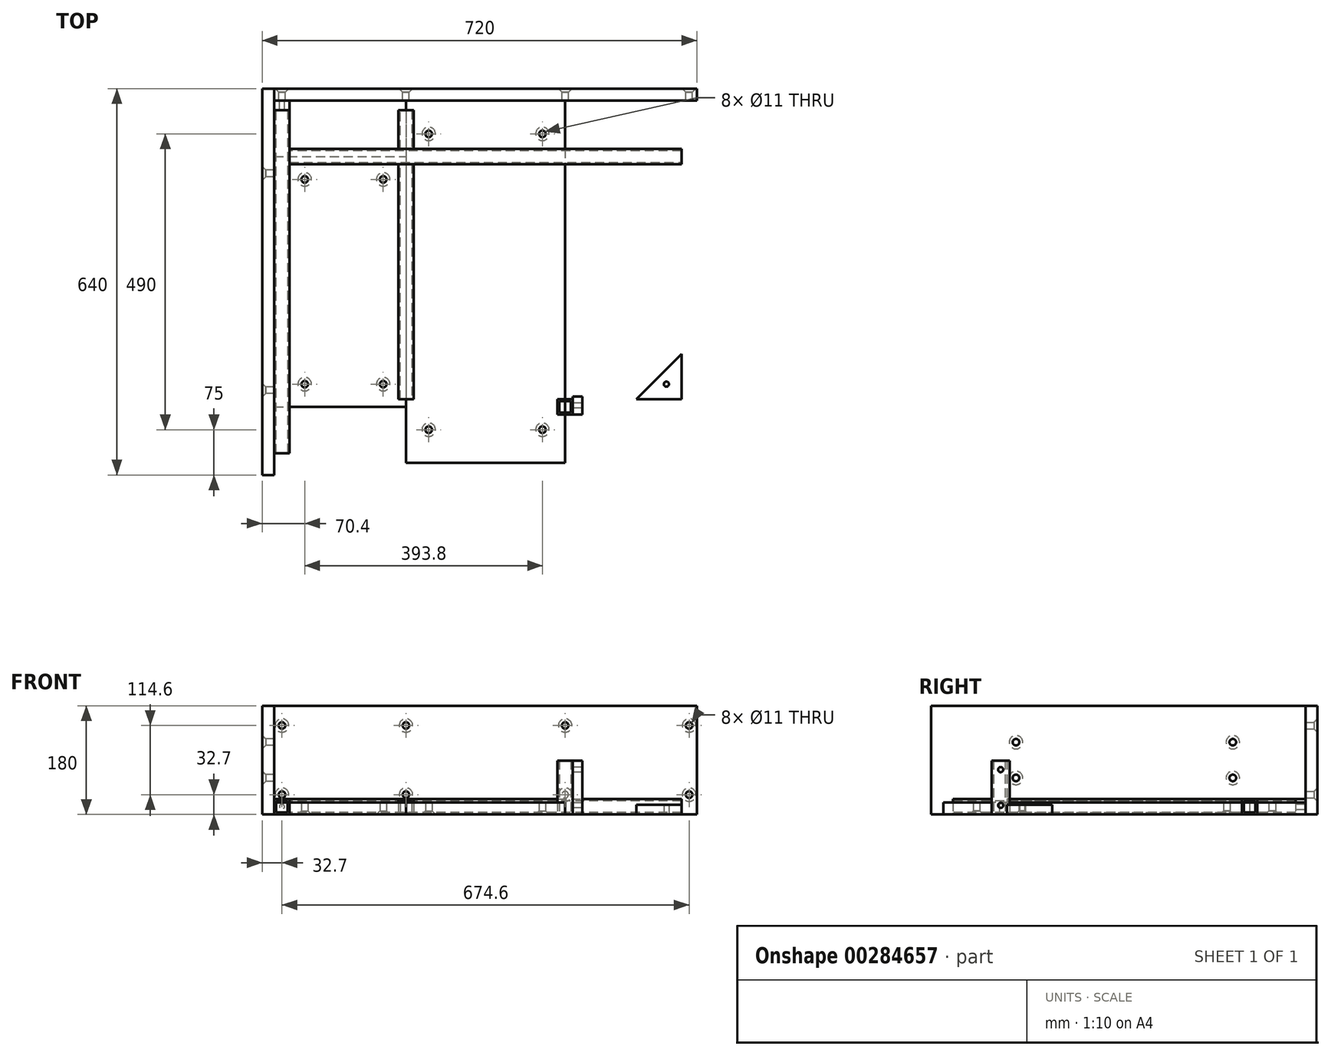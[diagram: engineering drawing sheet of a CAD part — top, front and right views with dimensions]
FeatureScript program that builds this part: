
annotation { "Feature Type Name" : "Feature", "Feature Type Description" : "" }
export const myFeature = defineFeature(function(context is Context, id is Id, definition is map)
    precondition{}
    {
        {
            var Q0;
            Q0=qCreatedBy(makeId("Top.planeOp"),FACE);
            var sketch = newSketch(context, id + "F0", { "sketchPlane" : qUnion([Q0])});
            skLineSegment(sketch, "E0.bottom", {"start": v(350, -300) * mm, "end": v(-350, -300) * mm});
            skLineSegment(sketch, "E0.top", {"start": v(350, 300) * mm, "end": v(-350, 300) * mm});
            skLineSegment(sketch, "E0.left", {"start": v(350, -300) * mm, "end": v(350, 300) * mm});
            skLineSegment(sketch, "E0.right", {"start": v(-350, -300) * mm, "end": v(-350, 300) * mm});
            skPoint(sketch, "E0.middle", {"position": v(0, 0) * mm});
            skLineSegment(sketch, "E1", {"start": v(-324.6, 300) * mm, "end": v(-324.6, -300) * mm});
            skLineSegment(sketch, "E2", {"start": v(324.6, 300) * mm, "end": v(324.6, -300) * mm});
            skLineSegment(sketch, "E3", {"start": v(324.6, 220) * mm, "end": v(-324.6, 220) * mm});
            skLineSegment(sketch, "E4", {"start": v(-324.6, 194.6) * mm, "end": v(324.6, 194.6) * mm});
            skLineSegment(sketch, "E5", {"start": v(-119.2, 300) * mm, "end": v(-119.2, 220) * mm});
            skPoint(sketch, "E5.endSnap0", {"position": v(0, 220) * mm});
            skLineSegment(sketch, "E6", {"start": v(-144.6, 220) * mm, "end": v(-144.6, 300) * mm});
            skLineSegment(sketch, "E7.MirrorCS", {"start": v(119.2, 300) * mm, "end": v(119.2, 220) * mm});
            skLineSegment(sketch, "E8.MirrorCS", {"start": v(144.6, 220) * mm, "end": v(144.6, 300) * mm});
            skLineSegment(sketch, "E9", {"start": v(-350, 284) * mm, "end": v(350, 284) * mm});
            skLineSegment(sketch, "E10.MirrorCS", {"start": v(-324.6, -194.6) * mm, "end": v(324.6, -194.6) * mm});
            skLineSegment(sketch, "E11.MirrorCS", {"start": v(324.6, -220) * mm, "end": v(-324.6, -220) * mm});
            skLineSegment(sketch, "E12.MirrorCS", {"start": v(144.6, -220) * mm, "end": v(144.6, -300) * mm});
            skLineSegment(sketch, "E13.MirrorCS", {"start": v(119.2, -300) * mm, "end": v(119.2, -220) * mm});
            skLineSegment(sketch, "E14.MirrorCS", {"start": v(-119.2, -300) * mm, "end": v(-119.2, -220) * mm});
            skLineSegment(sketch, "E15.MirrorCS", {"start": v(-144.6, -220) * mm, "end": v(-144.6, -300) * mm});
            skLineSegment(sketch, "E16.MirrorCS", {"start": v(-350, -284) * mm, "end": v(350, -284) * mm});
            skLineSegment(sketch, "E17", {"start": v(-144.6, -194.6) * mm, "end": v(-144.6, 194.6) * mm});
            skLineSegment(sketch, "E18", {"start": v(-119.2, 194.6) * mm, "end": v(-119.2, -194.6) * mm});
            skLineSegment(sketch, "E19.MirrorCS", {"start": v(119.2, 194.6) * mm, "end": v(119.2, -194.6) * mm});
            skLineSegment(sketch, "E20.MirrorCS", {"start": v(144.6, -194.6) * mm, "end": v(144.6, 194.6) * mm});
            skSolve(sketch);
        }
        {
            var Q0;
            {var subQ3=sQuery(id+"F0.wireOp",EDGE,"E9");var subQ6=sQuery(id+"F0.wireOp",EDGE,"E0.right");var subQ7=makeQuery(id+"F0.imprint","INTERSECT",VERTEX,{"derivedFrom":[subQ6,subQ3]});Q0=makeQuery(id+"F0.imprint","IMPRINT",FACE,{"disambiguationData":[TD([[makeQuery(id+"F0.imprint","IMPRINT",EDGE,{"disambiguationData":[TD([[subQ7,1.0]])],"derivedFrom":subQ6}),-1.0]])]});}
            extrude(context, id + "F1", {"entities" : qUnion([Q0]), "depth" : 25.4 * mm});
        }
        {
            var Q0;
            {var subQ5=sQuery(id+"F0.wireOp",EDGE,"E4");Q0=makeQuery(id+"F0.imprint","IMPRINT",FACE,{"disambiguationData":[TD([[makeQuery(id+"F0.imprint","IMPRINT",EDGE,{"derivedFrom":subQ5}),1.0]])]});}
            extrude(context, id + "F2", {"entities" : qUnion([Q0]), "depth" : 25.4 * mm});
        }
        {
            var Q0;
            {var subQ0=sQuery(id+"F0.wireOp",EDGE,"E5");var subQ1=sQuery(id+"F0.wireOp",EDGE,"E3");var subQ2=makeQuery(id+"F0.imprint","INTERSECT",VERTEX,{"derivedFrom":[subQ1,subQ0]});Q0=makeQuery(id+"F0.imprint","IMPRINT",FACE,{"disambiguationData":[TD([[makeQuery(id+"F0.imprint","IMPRINT",EDGE,{"disambiguationData":[TD([[subQ2,-1.0]])],"derivedFrom":subQ1}),-1.0]])]});}
            extrude(context, id + "F3", {"entities" : qUnion([Q0]), "depth" : 25.4 * mm});
        }
        {
            var Q0;
            {var subQ0=sQuery(id+"F0.wireOp",EDGE,"E17");Q0=makeQuery(id+"F0.imprint","IMPRINT",FACE,{"disambiguationData":[TD([[makeQuery(id+"F0.imprint","IMPRINT",EDGE,{"derivedFrom":subQ0}),-1.0]])]});}
            extrude(context, id + "F4", {"entities" : qUnion([Q0]), "depth" : 25.4 * mm});
        }
        {
            var Q0;
            Q0=makeQuery(id+"F1.opExtrude","SWEPT_FACE",FACE,{"disambiguationData":[OSD([sQuery(id+"F0.wireOp",EDGE,"E9")])]});
            var Q1;
            Q1=makeQuery(id+"F1.opExtrude","SWEPT_FACE",FACE,{"disambiguationData":[OSD([sQuery(id+"F0.wireOp",EDGE,"E16.MirrorCS")])]});
            shell(context, id + "F5", {"entities" : qUnion([Q0, Q1]), "thickness" : 3.17 * mm});
        }
        {
            var Q0;
            Q0=makeQuery(id+"F2.opExtrude","SWEPT_FACE",FACE,{"disambiguationData":[OSD([sQuery(id+"F0.wireOp",EDGE,"E1")])]});
            var Q1;
            Q1=makeQuery(id+"F2.opExtrude","SWEPT_FACE",FACE,{"disambiguationData":[OSD([sQuery(id+"F0.wireOp",EDGE,"E2")])]});
            shell(context, id + "F6", {"entities" : qUnion([Q0, Q1]), "thickness" : 3.17 * mm});
        }
        {
            var Q0;
            Q0=makeQuery(id+"F3.opExtrude","SWEPT_FACE",FACE,{"disambiguationData":[OSD([sQuery(id+"F0.wireOp",EDGE,"E9")])]});
            var Q1;
            Q1=makeQuery(id+"F3.opExtrude","SWEPT_FACE",FACE,{"disambiguationData":[OSD([sQuery(id+"F0.wireOp",EDGE,"E3")])]});
            shell(context, id + "F7", {"entities" : qUnion([Q0, Q1]), "thickness" : 3.17 * mm});
        }
        {
            var Q0;
            Q0=makeQuery(id+"F4.opExtrude","SWEPT_FACE",FACE,{"disambiguationData":[OSD([sQuery(id+"F0.wireOp",EDGE,"E10.MirrorCS")])]});
            var Q1;
            Q1=makeQuery(id+"F4.opExtrude","SWEPT_FACE",FACE,{"disambiguationData":[OSD([sQuery(id+"F0.wireOp",EDGE,"E4")])]});
            shell(context, id + "F8", {"entities" : qUnion([Q0, Q1]), "thickness" : 3.17 * mm});
        }
        {
            var Q0;
            {var subQ0=sQuery(id+"F0.wireOp",EDGE,"E0.right");var subQ1=sQuery(id+"F0.wireOp",EDGE,"E0.top");var subQ2=makeQuery(id+"F0.imprint","INTERSECT",VERTEX,{"derivedFrom":[subQ1,subQ0]});Q0=makeQuery(id+"F0.imprint","IMPRINT",FACE,{"disambiguationData":[TD([[makeQuery(id+"F0.imprint","IMPRINT",EDGE,{"disambiguationData":[TD([[subQ2,1.0]])],"derivedFrom":subQ1}),1.0]])]});}
            extrude(context, id + "F9", {"entities" : qUnion([Q0]), "depth" : 25.4 * mm});
        }
        {
            var Q0;
            Q0=makeQuery(id+"F9.opExtrude","SWEPT_FACE",FACE,{"disambiguationData":[OSD([sQuery(id+"F0.wireOp",EDGE,"E0.top")])]});
            var sketch = newSketch(context, id + "F10", { "sketchPlane" : qUnion([Q0])});
            skLineSegment(sketch, "E21", {"start": v(324.6, 25.4) * mm, "end": v(350, 0) * mm});
            skPoint(sketch, "E22", {"position": v(337.3, 12.7) * mm});
            skSolve(sketch);
        }
        {
            var Q0;
            Q0=sQuery(id+"F10.wireOp",VERTEX,"E22");
            var Q1;
            Q1=makeQuery(id+"F9.opExtrude","SWEPT_BODY",BODY,{"disambiguationData":[OSD([sQuery(id+"F0.wireOp",EDGE,"E0.top"),sQuery(id+"F0.wireOp",EDGE,"E0.right"),sQuery(id+"F0.wireOp",EDGE,"E1"),sQuery(id+"F0.wireOp",EDGE,"E9")])]});
            hole(context, id + "F11", {"style" : HoleStyle.SIMPLE, "endStyle" : HoleEndStyle.THROUGH, "standardTappedOrClearance" : lookupTablePath({ "standard" : "ISO", "engagement" : "75%", "pitch" : "1.5 mm", "size" : "M10", "type" : "Tapped" }), "standardBlindInLast" : lookupTablePath({ "standard" : "ISO", "engagement" : "75%", "pitch" : "1.5 mm", "size" : "M10", "type" : "Tapped" }), "holeDiameter" : 8.5 * mm, "showTappedDepth" : true, "tappedDepth" : 12 * mm, "tapClearance" : 3, "locations" : qUnion([Q0]), "scope" : qUnion([Q1]), "majorDiameter" : 10 * mm});
        }
        {
            var Q0;
            Q0=qCreatedBy(makeId("Top.planeOp"),FACE);
            var sketch = newSketch(context, id + "F12", { "sketchPlane" : qUnion([Q0])});
            skLineSegment(sketch, "E23", {"start": v(249.6, -194.6) * mm, "end": v(324.6, -119.6) * mm});
            skLineSegment(sketch, "E24", {"start": v(324.6, -119.6) * mm, "end": v(324.6, -194.6) * mm});
            skLineSegment(sketch, "E25", {"start": v(324.6, -194.6) * mm, "end": v(249.6, -194.6) * mm});
            skPoint(sketch, "E26", {"position": v(299.6, -169.6) * mm});
            skSolve(sketch);
        }
        {
            var Q0;
            Q0 = qSketchRegion(id + "F12", true);
            extrude(context, id + "F13", {"entities" : qUnion([Q0]), "depth" : 16 * mm});
        }
        {
            var Q0;
            Q0=sQuery(id+"F12.wireOp",VERTEX,"E26");
            var Q1;
            Q1=makeQuery(id+"F13.opExtrude","SWEPT_BODY",BODY,{"disambiguationData":[OSD([sQuery(id+"F12.wireOp",EDGE,"E23"),sQuery(id+"F12.wireOp",EDGE,"E24"),sQuery(id+"F12.wireOp",EDGE,"E25")])]});
            hole(context, id + "F14", {"style" : HoleStyle.SIMPLE, "endStyle" : HoleEndStyle.THROUGH, "oppositeDirection" : true, "standardTappedOrClearance" : lookupTablePath({ "standard" : "ISO", "engagement" : "75%", "pitch" : "1.5 mm", "size" : "M10", "type" : "Tapped" }), "standardBlindInLast" : lookupTablePath({ "standard" : "ISO", "engagement" : "75%", "pitch" : "1.5 mm", "size" : "M10", "type" : "Tapped" }), "holeDiameter" : 8.5 * mm, "showTappedDepth" : true, "tappedDepth" : 12 * mm, "tapClearance" : 3, "locations" : qUnion([Q0]), "scope" : qUnion([Q1]), "majorDiameter" : 10 * mm});
        }
        {
            var Q0;
            {var subQ0=sQuery(id+"F0.wireOp",EDGE,"E18");Q0=makeQuery(id+"F0.imprint","IMPRINT",FACE,{"disambiguationData":[TD([[makeQuery(id+"F0.imprint","IMPRINT",EDGE,{"derivedFrom":subQ0}),1.0]])]});}
            var sketch = newSketch(context, id + "F15", { "sketchPlane" : qUnion([Q0])});
            skLineSegment(sketch, "E27.bottom", {"start": v(-350, 300) * mm, "end": v(350, 300) * mm});
            skLineSegment(sketch, "E27.top", {"start": v(-350, 320) * mm, "end": v(350, 320) * mm});
            skLineSegment(sketch, "E27.left", {"start": v(-350, 300) * mm, "end": v(-350, 320) * mm});
            skLineSegment(sketch, "E27.right", {"start": v(350, 300) * mm, "end": v(350, 320) * mm});
            skSolve(sketch);
        }
        {
            var Q0;
            Q0=makeQuery(id+"F15.imprint","IMPRINT",FACE,{"disambiguationData":[TD([[makeQuery(id+"F15.imprint","IMPRINT",EDGE,{"derivedFrom":sQuery(id+"F15.wireOp",EDGE,"E27.bottom")}),1.0]])]});
            extrude(context, id + "F16", {"entities" : qUnion([Q0]), "depth" : 180 * mm});
        }
        {
            var Q0;
            Q0=makeQuery(id+"F16.opExtrude","SWEPT_FACE",FACE,{"disambiguationData":[OSD([sQuery(id+"F15.wireOp",EDGE,"E27.top")])]});
            var sketch = newSketch(context, id + "F17", { "sketchPlane" : qUnion([Q0])});
            skPoint(sketch, "E28", {"position": v(-337.3, 32.7) * mm});
            skPoint(sketch, "E29", {"position": v(-131.9, 32.7) * mm});
            skPoint(sketch, "E30.MirrorP", {"position": v(131.9, 32.7) * mm});
            skPoint(sketch, "E31.MirrorP", {"position": v(337.3, 32.7) * mm});
            skLineSegment(sketch, "E32", {"start": v(-350, 90) * mm, "end": v(350, 90) * mm});
            skPoint(sketch, "E33.MirrorP", {"position": v(-131.9, 147.3) * mm});
            skPoint(sketch, "E34.MirrorP", {"position": v(-337.3, 147.3) * mm});
            skPoint(sketch, "E35.MirrorP", {"position": v(131.9, 147.3) * mm});
            skPoint(sketch, "E36.MirrorP", {"position": v(337.3, 147.3) * mm});
            skSolve(sketch);
        }
        {
            var Q0;
            Q0=sQuery(id+"F17.wireOp",VERTEX,"E33.MirrorP");
            var Q1;
            Q1=sQuery(id+"F17.wireOp",VERTEX,"E29");
            var Q2;
            Q2=sQuery(id+"F17.wireOp",VERTEX,"E34.MirrorP");
            var Q3;
            Q3=sQuery(id+"F17.wireOp",VERTEX,"E28");
            var Q4;
            Q4=sQuery(id+"F17.wireOp",VERTEX,"E35.MirrorP");
            var Q5;
            Q5=sQuery(id+"F17.wireOp",VERTEX,"E30.MirrorP");
            var Q6;
            Q6=sQuery(id+"F17.wireOp",VERTEX,"E36.MirrorP");
            var Q7;
            Q7=sQuery(id+"F17.wireOp",VERTEX,"E31.MirrorP");
            var Q8;
            Q8=makeQuery(id+"F16.opExtrude","SWEPT_BODY",BODY,{"disambiguationData":[OSD([sQuery(id+"F15.wireOp",EDGE,"E27.bottom"),sQuery(id+"F15.wireOp",EDGE,"E27.top"),sQuery(id+"F15.wireOp",EDGE,"E27.left"),sQuery(id+"F15.wireOp",EDGE,"E27.right")])]});
            hole(context, id + "F18", {"style" : HoleStyle.C_SINK, "endStyle" : HoleEndStyle.THROUGH, "standardTappedOrClearance" : lookupTablePath({ "standard" : "ISO", "fit" : "Normal", "size" : "M10", "type" : "Clearance" }), "standardBlindInLast" : lookupTablePath({ "fit" : "Standard", "standard" : "ISO", "size" : "M10", "type" : "Clearance" }), "holeDiameter" : 11 * mm, "cSinkDiameter" : 22.4 * mm, "cSinkAngle" : 90 * degree, "tappedDepth" : 12 * mm, "tapClearance" : 3, "locations" : qUnion([Q0, Q1, Q2, Q3, Q4, Q5, Q6, Q7]), "scope" : qUnion([Q8])});
        }
        {
            var Q0;
            Q0=qCreatedBy(makeId("Top.planeOp"),FACE);
            var sketch = newSketch(context, id + "F19", { "sketchPlane" : qUnion([Q0])});
            skLineSegment(sketch, "E37.bottom", {"start": v(-370, -320) * mm, "end": v(-350, -320) * mm});
            skLineSegment(sketch, "E37.top", {"start": v(-370, 320) * mm, "end": v(-350, 320) * mm});
            skLineSegment(sketch, "E37.left", {"start": v(-370, -320) * mm, "end": v(-370, 320) * mm});
            skLineSegment(sketch, "E37.right", {"start": v(-350, -320) * mm, "end": v(-350, 320) * mm});
            skSolve(sketch);
        }
        {
            var Q0;
            Q0 = qSketchRegion(id + "F19", true);
            extrude(context, id + "F20", {"entities" : qUnion([Q0]), "depth" : 180 * mm});
        }
        {
            var Q0;
            Q0=qCreatedBy(makeId("Top.planeOp"),FACE);
            var sketch = newSketch(context, id + "F21", { "sketchPlane" : qUnion([Q0])});
            skLineSegment(sketch, "E38.bottom", {"start": v(-350, -300) * mm, "end": v(350, -300) * mm});
            skLineSegment(sketch, "E38.top", {"start": v(-350, 300) * mm, "end": v(350, 300) * mm});
            skLineSegment(sketch, "E38.left", {"start": v(-350, -300) * mm, "end": v(-350, 300) * mm});
            skLineSegment(sketch, "E38.right", {"start": v(350, -300) * mm, "end": v(350, 300) * mm});
            skLineSegment(sketch, "E39", {"start": v(-350, 207.3) * mm, "end": v(350, 207.3) * mm});
            skLineSegment(sketch, "E40.MirrorCS", {"start": v(-350, -207.3) * mm, "end": v(350, -207.3) * mm});
            skLineSegment(sketch, "E41", {"start": v(-131.9, 300) * mm, "end": v(-131.9, -300) * mm});
            skLineSegment(sketch, "E42.MirrorCS", {"start": v(131.9, 300) * mm, "end": v(131.9, -300) * mm});
            skPoint(sketch, "E43", {"position": v(-299.6, 169.6) * mm});
            skPoint(sketch, "E44", {"position": v(-299.6, -169.6) * mm});
            skPoint(sketch, "E45", {"position": v(-169.6, -169.6) * mm});
            skPoint(sketch, "E46", {"position": v(-169.6, 169.6) * mm});
            skPoint(sketch, "E47", {"position": v(169.6, -169.6) * mm});
            skPoint(sketch, "E48", {"position": v(169.6, 169.6) * mm});
            skPoint(sketch, "E49", {"position": v(299.6, 169.6) * mm});
            skPoint(sketch, "E50", {"position": v(299.6, -169.6) * mm});
            skPoint(sketch, "E51", {"position": v(-94.2, 245) * mm});
            skPoint(sketch, "E52.MirrorP", {"position": v(94.2, 245) * mm});
            skPoint(sketch, "E53.MirrorP", {"position": v(94.2, -245) * mm});
            skPoint(sketch, "E54.MirrorP", {"position": v(-94.2, -245) * mm});
            skSolve(sketch);
        }
        {
            var Q0;
            {var subQ0=sQuery(id+"F21.wireOp",EDGE,"E39");var subQ1=sQuery(id+"F21.wireOp",EDGE,"E38.left");var subQ2=makeQuery(id+"F21.imprint","INTERSECT",VERTEX,{"derivedFrom":[subQ1,subQ0]});Q0=makeQuery(id+"F21.imprint","IMPRINT",FACE,{"disambiguationData":[TD([[makeQuery(id+"F21.imprint","IMPRINT",EDGE,{"disambiguationData":[TD([[subQ2,1.0]])],"derivedFrom":subQ1}),-1.0]])]});}
            extrude(context, id + "F22", {"entities" : qUnion([Q0]), "depth" : 20 * mm});
        }
        {
            var Q0;
            {var subQ0=sQuery(id+"F21.wireOp",EDGE,"E41");var subQ1=sQuery(id+"F21.wireOp",EDGE,"E38.top");var subQ2=makeQuery(id+"F21.imprint","INTERSECT",VERTEX,{"derivedFrom":[subQ1,subQ0]});Q0=makeQuery(id+"F21.imprint","IMPRINT",FACE,{"disambiguationData":[TD([[makeQuery(id+"F21.imprint","IMPRINT",EDGE,{"disambiguationData":[TD([[subQ2,-1.0]])],"derivedFrom":subQ1}),-1.0]])]});}
            var Q1;
            {var subQ0=sQuery(id+"F21.wireOp",EDGE,"E41");var subQ1=sQuery(id+"F21.wireOp",EDGE,"E39");var subQ2=makeQuery(id+"F21.imprint","INTERSECT",VERTEX,{"derivedFrom":[subQ1,subQ0]});Q1=makeQuery(id+"F21.imprint","IMPRINT",FACE,{"disambiguationData":[TD([[makeQuery(id+"F21.imprint","IMPRINT",EDGE,{"disambiguationData":[TD([[subQ2,-1.0]])],"derivedFrom":subQ1}),-1.0]])]});}
            var Q2;
            {var subQ0=sQuery(id+"F21.wireOp",EDGE,"E41");var subQ1=sQuery(id+"F21.wireOp",EDGE,"E38.bottom");var subQ2=makeQuery(id+"F21.imprint","INTERSECT",VERTEX,{"derivedFrom":[subQ1,subQ0]});Q2=makeQuery(id+"F21.imprint","IMPRINT",FACE,{"disambiguationData":[TD([[makeQuery(id+"F21.imprint","IMPRINT",EDGE,{"disambiguationData":[TD([[subQ2,-1.0]])],"derivedFrom":subQ1}),1.0]])]});}
            extrude(context, id + "F23", {"entities" : qUnion([Q0, Q1, Q2]), "depth" : 20 * mm});
        }
        {
            var Q0;
            Q0=sQuery(id+"F21.wireOp",VERTEX,"E43");
            var Q1;
            Q1=sQuery(id+"F21.wireOp",VERTEX,"E46");
            var Q2;
            Q2=sQuery(id+"F21.wireOp",VERTEX,"E45");
            var Q3;
            Q3=sQuery(id+"F21.wireOp",VERTEX,"E44");
            var Q4;
            Q4=makeQuery(id+"F22.opExtrude","SWEPT_BODY",BODY,{"disambiguationData":[OSD([sQuery(id+"F21.wireOp",EDGE,"E38.left"),sQuery(id+"F21.wireOp",EDGE,"E39"),sQuery(id+"F21.wireOp",EDGE,"E40.MirrorCS"),sQuery(id+"F21.wireOp",EDGE,"E41")])]});
            hole(context, id + "F24", {"style" : HoleStyle.C_SINK, "endStyle" : HoleEndStyle.THROUGH, "oppositeDirection" : true, "standardTappedOrClearance" : lookupTablePath({ "standard" : "ISO", "fit" : "Normal", "size" : "M10", "type" : "Clearance" }), "standardBlindInLast" : lookupTablePath({ "fit" : "Standard", "standard" : "ISO", "size" : "M10", "type" : "Clearance" }), "holeDiameter" : 11 * mm, "cSinkDiameter" : 22.4 * mm, "cSinkAngle" : 90 * degree, "tappedDepth" : 12 * mm, "tapClearance" : 3, "locations" : qUnion([Q0, Q1, Q2, Q3]), "scope" : qUnion([Q4])});
        }
        {
            var Q0;
            Q0=sQuery(id+"F21.wireOp",VERTEX,"E51");
            var Q1;
            Q1=sQuery(id+"F21.wireOp",VERTEX,"E52.MirrorP");
            var Q2;
            Q2=sQuery(id+"F21.wireOp",VERTEX,"E54.MirrorP");
            var Q3;
            Q3=sQuery(id+"F21.wireOp",VERTEX,"E53.MirrorP");
            var Q4;
            Q4=makeQuery(id+"F23.opExtrude","SWEPT_BODY",BODY,{"disambiguationData":[OSD([sQuery(id+"F21.wireOp",EDGE,"E38.bottom"),sQuery(id+"F21.wireOp",EDGE,"E38.top"),sQuery(id+"F21.wireOp",EDGE,"E41"),sQuery(id+"F21.wireOp",EDGE,"E42.MirrorCS")])]});
            hole(context, id + "F25", {"style" : HoleStyle.C_SINK, "endStyle" : HoleEndStyle.THROUGH, "oppositeDirection" : true, "standardTappedOrClearance" : lookupTablePath({ "standard" : "ISO", "fit" : "Normal", "size" : "M10", "type" : "Clearance" }), "standardBlindInLast" : lookupTablePath({ "fit" : "Standard", "standard" : "ISO", "size" : "M10", "type" : "Clearance" }), "holeDiameter" : 11 * mm, "cSinkDiameter" : 22.4 * mm, "cSinkAngle" : 90 * degree, "tappedDepth" : 12 * mm, "tapClearance" : 3, "locations" : qUnion([Q0, Q1, Q2, Q3]), "scope" : qUnion([Q4])});
        }
        {
            var Q0;
            Q0=qCreatedBy(makeId("Top.planeOp"),FACE);
            var sketch = newSketch(context, id + "F26", { "sketchPlane" : qUnion([Q0])});
            skLineSegment(sketch, "E55.bottom", {"start": v(144.6, -220) * mm, "end": v(119.2, -220) * mm});
            skLineSegment(sketch, "E55.top", {"start": v(144.6, -194.6) * mm, "end": v(119.2, -194.6) * mm});
            skLineSegment(sketch, "E55.left", {"start": v(144.6, -220) * mm, "end": v(144.6, -194.6) * mm});
            skLineSegment(sketch, "E55.right", {"start": v(119.2, -220) * mm, "end": v(119.2, -194.6) * mm});
            skSolve(sketch);
        }
        {
            var Q0;
            Q0 = qSketchRegion(id + "F26", true);
            extrude(context, id + "F27", {"entities" : qUnion([Q0]), "depth" : (140 - 50.8) * mm});
        }
        {
            var Q0;
            Q0=makeQuery(id+"F27.opExtrude","CAP_FACE",FACE,{"disambiguationData":[OSD([sQuery(id+"F26.wireOp",EDGE,"E55.bottom"),sQuery(id+"F26.wireOp",EDGE,"E55.top"),sQuery(id+"F26.wireOp",EDGE,"E55.left"),sQuery(id+"F26.wireOp",EDGE,"E55.right")])],"isStart":false});
            var Q1;
            Q1=makeQuery(id+"F27.opExtrude","CAP_FACE",FACE,{"disambiguationData":[OSD([sQuery(id+"F26.wireOp",EDGE,"E55.bottom"),sQuery(id+"F26.wireOp",EDGE,"E55.top"),sQuery(id+"F26.wireOp",EDGE,"E55.left"),sQuery(id+"F26.wireOp",EDGE,"E55.right")])],"isStart":true});
            shell(context, id + "F28", {"entities" : qUnion([Q0, Q1]), "thickness" : 3.17 * mm});
        }
        {
            var Q0;
            Q0=makeQuery(id+"F27.opExtrude","SWEPT_FACE",FACE,{"disambiguationData":[OSD([sQuery(id+"F26.wireOp",EDGE,"E55.left")])]});
            var sketch = newSketch(context, id + "F29", { "sketchPlane" : qUnion([Q0])});
            skLineSegment(sketch, "E56.bottom", {"start": v(-220, 89.2) * mm, "end": v(-190, 89.2) * mm});
            skLineSegment(sketch, "E56.top", {"start": v(-220, 0) * mm, "end": v(-190, 0) * mm});
            skLineSegment(sketch, "E56.left", {"start": v(-220, 89.2) * mm, "end": v(-220, 0) * mm});
            skLineSegment(sketch, "E56.right", {"start": v(-190, 89.2) * mm, "end": v(-190, 0) * mm});
            skPoint(sketch, "E57", {"position": v(-205, 74.2) * mm});
            skPoint(sketch, "E57.positionSnap0", {"position": v(-205, 89.2) * mm});
            skPoint(sketch, "E58", {"position": v(-205, 15) * mm});
            skSolve(sketch);
        }
        {
            var Q0;
            Q0=makeQuery(id+"F29.imprint","IMPRINT",FACE,{"disambiguationData":[TD([[makeQuery(id+"F29.imprint","IMPRINT",EDGE,{"derivedFrom":sQuery(id+"F29.wireOp",EDGE,"E56.bottom")}),-1.0]])]});
            extrude(context, id + "F30", {"entities" : qUnion([Q0]), "depth" : 16 * mm});
        }
        {
            var Q0;
            Q0=sQuery(id+"F29.wireOp",VERTEX,"E57");
            var Q1;
            Q1=sQuery(id+"F29.wireOp",VERTEX,"E58");
            var Q2;
            Q2=makeQuery(id+"F30.opExtrude","SWEPT_BODY",BODY,{"disambiguationData":[OSD([sQuery(id+"F29.wireOp",EDGE,"E56.bottom"),sQuery(id+"F29.wireOp",EDGE,"E56.top"),sQuery(id+"F29.wireOp",EDGE,"E56.left"),sQuery(id+"F29.wireOp",EDGE,"E56.right")])]});
            hole(context, id + "F31", {"style" : HoleStyle.SIMPLE, "endStyle" : HoleEndStyle.THROUGH, "oppositeDirection" : true, "standardTappedOrClearance" : lookupTablePath({ "standard" : "ISO", "engagement" : "75%", "pitch" : "1.5 mm", "size" : "M10", "type" : "Tapped" }), "standardBlindInLast" : lookupTablePath({ "standard" : "ISO", "engagement" : "75%", "pitch" : "1.5 mm", "size" : "M10", "type" : "Tapped" }), "holeDiameter" : 8.5 * mm, "showTappedDepth" : true, "tappedDepth" : 12 * mm, "tapClearance" : 3, "locations" : qUnion([Q0, Q1]), "scope" : qUnion([Q2]), "majorDiameter" : 10 * mm});
        }
        {
            var Q0;
            Q0=makeQuery(id+"F20.opExtrude","SWEPT_FACE",FACE,{"disambiguationData":[OSD([sQuery(id+"F19.wireOp",EDGE,"E37.left")])]});
            var sketch = newSketch(context, id + "F32", { "sketchPlane" : qUnion([Q0])});
            skLineSegment(sketch, "E59.bottom", {"start": v(-179.6, 119.6) * mm, "end": v(179.6, 119.6) * mm});
            skLineSegment(sketch, "E59.top", {"start": v(-179.6, 60.4) * mm, "end": v(179.6, 60.4) * mm});
            skLineSegment(sketch, "E59.left", {"start": v(-179.6, 119.6) * mm, "end": v(-179.6, 60.4) * mm});
            skLineSegment(sketch, "E59.right", {"start": v(179.6, 119.6) * mm, "end": v(179.6, 60.4) * mm});
            skLineSegment(sketch, "E60", {"start": v(0, 119.6) * mm, "end": v(0, 180) * mm});
            skLineSegment(sketch, "E61", {"start": v(-320, 90) * mm, "end": v(-179.6, 90) * mm});
            skSolve(sketch);
        }
        {
            var Q0;
            Q0=sQuery(id+"F32.wireOp",VERTEX,"E59.left.start");
            var Q1;
            Q1=sQuery(id+"F32.wireOp",VERTEX,"E59.left.end");
            var Q2;
            Q2=sQuery(id+"F32.wireOp",VERTEX,"E59.right.start");
            var Q3;
            Q3=sQuery(id+"F32.wireOp",VERTEX,"E59.right.end");
            var Q4;
            Q4=makeQuery(id+"F20.opExtrude","SWEPT_BODY",BODY,{"disambiguationData":[OSD([sQuery(id+"F19.wireOp",EDGE,"E37.bottom"),sQuery(id+"F19.wireOp",EDGE,"E37.top"),sQuery(id+"F19.wireOp",EDGE,"E37.left"),sQuery(id+"F19.wireOp",EDGE,"E37.right")])]});
            hole(context, id + "F33", {"style" : HoleStyle.C_SINK, "endStyle" : HoleEndStyle.THROUGH, "standardTappedOrClearance" : lookupTablePath({ "standard" : "ISO", "fit" : "Normal", "size" : "M10", "type" : "Clearance" }), "standardBlindInLast" : lookupTablePath({ "fit" : "Standard", "standard" : "ISO", "size" : "M10", "type" : "Clearance" }), "holeDiameter" : 11 * mm, "cSinkDiameter" : 22.4 * mm, "cSinkAngle" : 90 * degree, "tappedDepth" : 12 * mm, "tapClearance" : 3, "locations" : qUnion([Q0, Q1, Q2, Q3]), "scope" : qUnion([Q4])});
        }
    });
